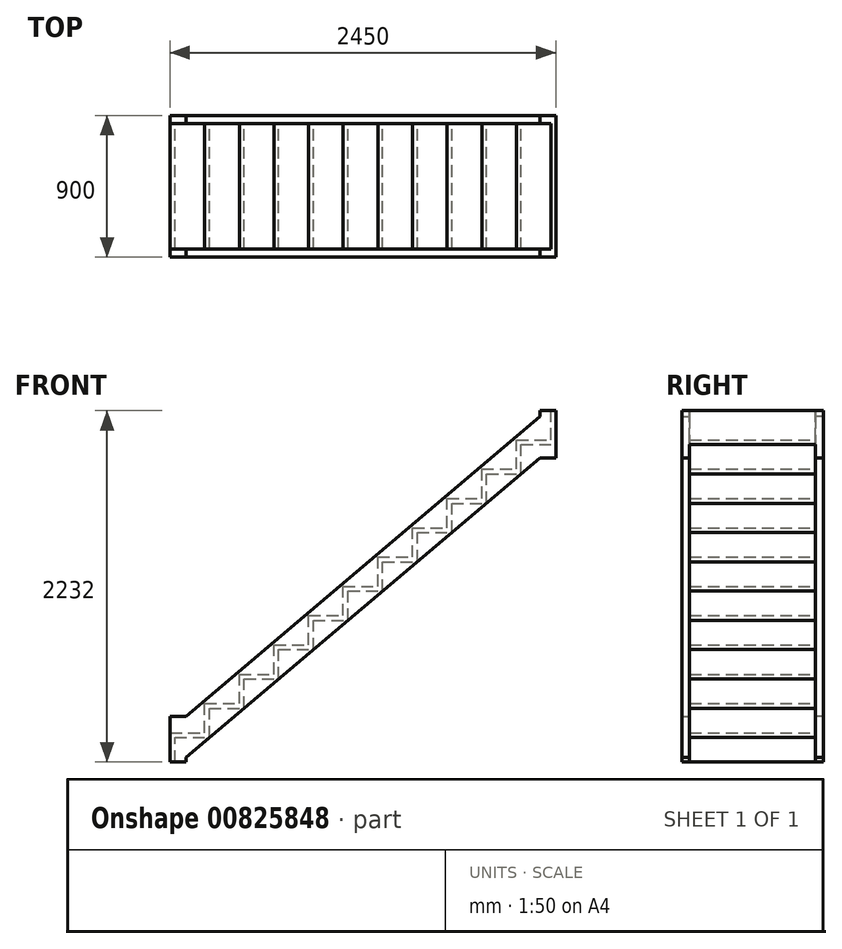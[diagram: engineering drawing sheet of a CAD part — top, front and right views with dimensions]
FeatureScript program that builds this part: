
annotation { "Feature Type Name" : "Feature", "Feature Type Description" : "" }
export const myFeature = defineFeature(function(context is Context, id is Id, definition is map)
    precondition{}
    {
        {
            var Q0;
            Q0=qCreatedBy(makeId("Front.planeOp"),FACE);
            var sketch = newSketch(context, id + "F0", { "sketchPlane" : qUnion([Q0])});
            skLineSegment(sketch, "E0", {"start": v(0, 0) * mm, "end": v(30, 0) * mm});
            skLineSegment(sketch, "E1.0", {"start": v(0, 186) * mm, "end": v(250, 186) * mm});
            skLineSegment(sketch, "E2.0", {"start": v(220, 186) * mm, "end": v(220, 372) * mm});
            skLineSegment(sketch, "E3.0", {"start": v(0, 0) * mm, "end": v(0, 186) * mm});
            skLineSegment(sketch, "E4.0", {"start": v(30, 0) * mm, "end": v(30, 156) * mm});
            skLineSegment(sketch, "E5.0", {"start": v(0, 156) * mm, "end": v(250, 156) * mm});
            skLineSegment(sketch, "E6.0", {"start": v(250, 156) * mm, "end": v(250, 342) * mm});
            skLineSegment(sketch, "E7.trimOffspring", {"start": v(220, 342) * mm, "end": v(470, 342) * mm});
            skLineSegment(sketch, "E8.trimOffspring", {"start": v(220, 372) * mm, "end": v(470, 372) * mm});
            skLineSegment(sketch, "E9.trimOffspring", {"start": v(440, 528) * mm, "end": v(690, 528) * mm});
            skLineSegment(sketch, "E10.trimOffspring", {"start": v(440, 558) * mm, "end": v(690, 558) * mm});
            skLineSegment(sketch, "E11.trimOffspring", {"start": v(660, 714) * mm, "end": v(910, 714) * mm});
            skLineSegment(sketch, "E12.trimOffspring", {"start": v(660, 744) * mm, "end": v(910, 744) * mm});
            skLineSegment(sketch, "E13.trimOffspring", {"start": v(880, 900) * mm, "end": v(1130, 900) * mm});
            skLineSegment(sketch, "E14.trimOffspring", {"start": v(880, 930) * mm, "end": v(1130, 930) * mm});
            skLineSegment(sketch, "E15.trimOffspring", {"start": v(1100, 1086) * mm, "end": v(1350, 1086) * mm});
            skLineSegment(sketch, "E16.trimOffspring", {"start": v(1100, 1116) * mm, "end": v(1350, 1116) * mm});
            skLineSegment(sketch, "E17.trimOffspring", {"start": v(1320, 1272) * mm, "end": v(1570, 1272) * mm});
            skLineSegment(sketch, "E18.trimOffspring", {"start": v(1320, 1302) * mm, "end": v(1570, 1302) * mm});
            skLineSegment(sketch, "E19.trimOffspring", {"start": v(1540, 1458) * mm, "end": v(1790, 1458) * mm});
            skLineSegment(sketch, "E20.trimOffspring", {"start": v(1540, 1488) * mm, "end": v(1790, 1488) * mm});
            skLineSegment(sketch, "E21.trimOffspring", {"start": v(1760, 1644) * mm, "end": v(2010, 1644) * mm});
            skLineSegment(sketch, "E22.trimOffspring", {"start": v(1760, 1674) * mm, "end": v(2010, 1674) * mm});
            skLineSegment(sketch, "E23.trimOffspring", {"start": v(1980, 1830) * mm, "end": v(2230, 1830) * mm});
            skLineSegment(sketch, "E24.trimOffspring", {"start": v(1980, 1860) * mm, "end": v(2230, 1860) * mm});
            skLineSegment(sketch, "E25.trimOffspring", {"start": v(2200, 2046) * mm, "end": v(2420, 2046) * mm});
            skLineSegment(sketch, "E26.trimOffspring", {"start": v(440, 372) * mm, "end": v(440, 558) * mm});
            skLineSegment(sketch, "E27.trimOffspring", {"start": v(470, 342) * mm, "end": v(470, 528) * mm});
            skLineSegment(sketch, "E28.trimOffspring", {"start": v(660, 558) * mm, "end": v(660, 744) * mm});
            skLineSegment(sketch, "E29.trimOffspring", {"start": v(690, 528) * mm, "end": v(690, 714) * mm});
            skLineSegment(sketch, "E30.trimOffspring", {"start": v(880, 744) * mm, "end": v(880, 930) * mm});
            skLineSegment(sketch, "E31.trimOffspring", {"start": v(910, 714) * mm, "end": v(910, 900) * mm});
            skLineSegment(sketch, "E32.trimOffspring", {"start": v(1100, 930) * mm, "end": v(1100, 1116) * mm});
            skLineSegment(sketch, "E33.trimOffspring", {"start": v(1130, 900) * mm, "end": v(1130, 1086) * mm});
            skLineSegment(sketch, "E34.trimOffspring", {"start": v(1320, 1116) * mm, "end": v(1320, 1302) * mm});
            skLineSegment(sketch, "E35.trimOffspring", {"start": v(1350, 1086) * mm, "end": v(1350, 1272) * mm});
            skLineSegment(sketch, "E36.trimOffspring", {"start": v(1540, 1302) * mm, "end": v(1540, 1488) * mm});
            skLineSegment(sketch, "E37.trimOffspring", {"start": v(1570, 1272) * mm, "end": v(1570, 1458) * mm});
            skLineSegment(sketch, "E38.trimOffspring", {"start": v(1760, 1488) * mm, "end": v(1760, 1674) * mm});
            skLineSegment(sketch, "E39.trimOffspring", {"start": v(1790, 1458) * mm, "end": v(1790, 1644) * mm});
            skLineSegment(sketch, "E40.trimOffspring", {"start": v(1980, 1674) * mm, "end": v(1980, 1860) * mm});
            skLineSegment(sketch, "E41.trimOffspring", {"start": v(2010, 1644) * mm, "end": v(2010, 1830) * mm});
            skLineSegment(sketch, "E42.trimOffspring", {"start": v(2200, 1860) * mm, "end": v(2200, 2046) * mm});
            skLineSegment(sketch, "E43.trimOffspring", {"start": v(2230, 1830) * mm, "end": v(2230, 2016) * mm});
            skLineSegment(sketch, "E44.trimOffspring", {"start": v(2420, 2046) * mm, "end": v(2420, 2232) * mm});
            skLineSegment(sketch, "E45.0", {"start": v(2200, 2016) * mm, "end": v(2420, 2016) * mm});
            skLineSegment(sketch, "E46.0", {"start": v(2450, 2046) * mm, "end": v(2450, 2232) * mm});
            skLineSegment(sketch, "E47", {"start": v(2420, 2046) * mm, "end": v(2450, 2046) * mm});
            skLineSegment(sketch, "E48", {"start": v(2450, 2016) * mm, "end": v(2420, 2016) * mm});
            skLineSegment(sketch, "E49", {"start": v(2450, 2046) * mm, "end": v(2450, 2016) * mm});
            skLineSegment(sketch, "E50", {"start": v(2450, 2232) * mm, "end": v(2420, 2232) * mm});
            skSolve(sketch);
        }
        {
            var Q0;
            Q0 = qSketchRegion(id + "F0", true);
            extrude(context, id + "F1", {"entities" : qUnion([Q0]), "depth" : 800 * mm, "offsetDistance" : 25 * mm});
        }
        {
            var Q0;
            Q0=makeQuery(id+"F1.opExtrude","CAP_FACE",FACE,{"disambiguationData":[OSD([sQuery(id+"F0.wireOp",EDGE,"E0"),sQuery(id+"F0.wireOp",EDGE,"E1.0"),sQuery(id+"F0.wireOp",EDGE,"E2.0"),sQuery(id+"F0.wireOp",EDGE,"E3.0"),sQuery(id+"F0.wireOp",EDGE,"E4.0"),sQuery(id+"F0.wireOp",EDGE,"E5.0"),sQuery(id+"F0.wireOp",EDGE,"E6.0"),sQuery(id+"F0.wireOp",EDGE,"E7.trimOffspring"),sQuery(id+"F0.wireOp",EDGE,"E8.trimOffspring"),sQuery(id+"F0.wireOp",EDGE,"E9.trimOffspring"),sQuery(id+"F0.wireOp",EDGE,"E10.trimOffspring"),sQuery(id+"F0.wireOp",EDGE,"E11.trimOffspring"),sQuery(id+"F0.wireOp",EDGE,"E12.trimOffspring"),sQuery(id+"F0.wireOp",EDGE,"E13.trimOffspring"),sQuery(id+"F0.wireOp",EDGE,"E14.trimOffspring"),sQuery(id+"F0.wireOp",EDGE,"E15.trimOffspring"),sQuery(id+"F0.wireOp",EDGE,"E16.trimOffspring"),sQuery(id+"F0.wireOp",EDGE,"E17.trimOffspring"),sQuery(id+"F0.wireOp",EDGE,"E18.trimOffspring"),sQuery(id+"F0.wireOp",EDGE,"E19.trimOffspring"),sQuery(id+"F0.wireOp",EDGE,"E20.trimOffspring"),sQuery(id+"F0.wireOp",EDGE,"E21.trimOffspring"),sQuery(id+"F0.wireOp",EDGE,"E22.trimOffspring"),sQuery(id+"F0.wireOp",EDGE,"E23.trimOffspring"),sQuery(id+"F0.wireOp",EDGE,"E24.trimOffspring"),sQuery(id+"F0.wireOp",EDGE,"E25.trimOffspring"),sQuery(id+"F0.wireOp",EDGE,"E26.trimOffspring"),sQuery(id+"F0.wireOp",EDGE,"E27.trimOffspring"),sQuery(id+"F0.wireOp",EDGE,"E28.trimOffspring"),sQuery(id+"F0.wireOp",EDGE,"E29.trimOffspring"),sQuery(id+"F0.wireOp",EDGE,"E30.trimOffspring"),sQuery(id+"F0.wireOp",EDGE,"E31.trimOffspring"),sQuery(id+"F0.wireOp",EDGE,"E32.trimOffspring"),sQuery(id+"F0.wireOp",EDGE,"E33.trimOffspring"),sQuery(id+"F0.wireOp",EDGE,"E34.trimOffspring"),sQuery(id+"F0.wireOp",EDGE,"E35.trimOffspring"),sQuery(id+"F0.wireOp",EDGE,"E36.trimOffspring"),sQuery(id+"F0.wireOp",EDGE,"E37.trimOffspring"),sQuery(id+"F0.wireOp",EDGE,"E38.trimOffspring"),sQuery(id+"F0.wireOp",EDGE,"E39.trimOffspring"),sQuery(id+"F0.wireOp",EDGE,"E40.trimOffspring"),sQuery(id+"F0.wireOp",EDGE,"E41.trimOffspring"),sQuery(id+"F0.wireOp",EDGE,"E42.trimOffspring"),sQuery(id+"F0.wireOp",EDGE,"E43.trimOffspring"),sQuery(id+"F0.wireOp",EDGE,"E44.trimOffspring"),sQuery(id+"F0.wireOp",EDGE,"E45.0"),sQuery(id+"F0.wireOp",EDGE,"E46.0"),sQuery(id+"F0.wireOp",EDGE,"E48"),sQuery(id+"F0.wireOp",EDGE,"E49"),sQuery(id+"F0.wireOp",EDGE,"E50")])],"isStart":false});
            var sketch = newSketch(context, id + "F2", { "sketchPlane" : qUnion([Q0])});
            skLineSegment(sketch, "E51", {"start": v(2420, 2232) * mm, "end": v(2450, 2232) * mm, "construction": true});
            skLineSegment(sketch, "E52", {"start": v(2450, 2232) * mm, "end": v(2450, 1931.45) * mm});
            skLineSegment(sketch, "E53", {"start": v(0, 0) * mm, "end": v(100, 0) * mm});
            skLineSegment(sketch, "E54.0", {"start": v(100, 186) * mm, "end": v(100, 0) * mm});
            skLineSegment(sketch, "E55", {"start": v(100, 186) * mm, "end": v(100, 291.08) * mm});
            skLineSegment(sketch, "E56.0", {"start": v(2350, 2232) * mm, "end": v(2350, 1931.45) * mm});
            skLineSegment(sketch, "E57", {"start": v(2350, 1931.45) * mm, "end": v(100, 29.18) * mm});
            skLineSegment(sketch, "E58.0", {"start": v(2350, 2062.4) * mm, "end": v(100, 160.13) * mm});
            skLineSegment(sketch, "E59.0", {"start": v(2350, 2193.35) * mm, "end": v(100, 291.08) * mm});
            skLineSegment(sketch, "E60", {"start": v(0, 291.08) * mm, "end": v(0, 0) * mm});
            skLineSegment(sketch, "E61", {"start": v(100, 291.08) * mm, "end": v(0, 291.08) * mm});
            skLineSegment(sketch, "E62", {"start": v(2450, 2232) * mm, "end": v(2350, 2232) * mm});
            skLineSegment(sketch, "E63", {"start": v(2350, 1931.45) * mm, "end": v(2450, 1931.45) * mm});
            skPoint(sketch, "E64.orphan", {"position": v(0, 446.74) * mm});
            skSolve(sketch);
        }
        {
            var Q0;
            Q0 = qSketchRegion(id + "F2", true);
            extrude(context, id + "F3", {"entities" : qUnion([Q0]), "operationType" : NewBodyOperationType.ADD, "depth" : 50 * mm, "offsetDistance" : 25 * mm});
        }
        {
            var Q0;
            {var subQ5=sQuery(id+"F0.wireOp",EDGE,"E25.trimOffspring");Q0=makeQuery(id+"F0.imprint","IMPRINT",FACE,{"disambiguationData":[TD([[makeQuery(id+"F0.imprint","IMPRINT",EDGE,{"derivedFrom":subQ5}),-1.0]])]});}
            var sketch = newSketch(context, id + "F4", { "sketchPlane" : qUnion([Q0])});
            skLineSegment(sketch, "E65", {"start": v(2420, 2232) * mm, "end": v(2450, 2232) * mm, "construction": true});
            skLineSegment(sketch, "E66", {"start": v(2450, 2232) * mm, "end": v(2450, 1931.45) * mm});
            skLineSegment(sketch, "E67", {"start": v(0, 0) * mm, "end": v(100, 0) * mm});
            skLineSegment(sketch, "E68.0", {"start": v(100, 186) * mm, "end": v(100, 0) * mm});
            skLineSegment(sketch, "E69", {"start": v(100, 186) * mm, "end": v(100, 291.08) * mm});
            skLineSegment(sketch, "E70.0", {"start": v(2350, 2232) * mm, "end": v(2350, 1931.45) * mm});
            skLineSegment(sketch, "E71", {"start": v(2350, 1931.45) * mm, "end": v(100, 29.18) * mm});
            skLineSegment(sketch, "E72.0", {"start": v(2350, 2062.4) * mm, "end": v(100, 160.13) * mm});
            skLineSegment(sketch, "E73.0", {"start": v(2350, 2193.35) * mm, "end": v(100, 291.08) * mm});
            skLineSegment(sketch, "E74", {"start": v(0, 291.08) * mm, "end": v(0, 0) * mm});
            skLineSegment(sketch, "E75", {"start": v(100, 291.08) * mm, "end": v(0, 291.08) * mm});
            skLineSegment(sketch, "E76", {"start": v(2450, 2232) * mm, "end": v(2350, 2232) * mm});
            skLineSegment(sketch, "E77", {"start": v(2350, 1931.45) * mm, "end": v(2450, 1931.45) * mm});
            skPoint(sketch, "E78.orphan", {"position": v(0, 446.74) * mm});
            skSolve(sketch);
        }
        {
            var Q0;
            Q0 = qSketchRegion(id + "F4", true);
            extrude(context, id + "F5", {"entities" : qUnion([Q0]), "operationType" : NewBodyOperationType.ADD, "oppositeDirection" : true, "depth" : 50 * mm, "offsetDistance" : 25 * mm});
        }
    });
